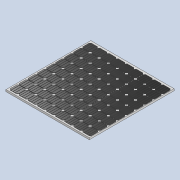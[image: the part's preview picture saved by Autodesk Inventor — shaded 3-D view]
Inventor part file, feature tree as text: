
AUTODESK INVENTOR PART (.ipt)
format: ipt  version: 2021 (Build 250183000, 183)  size: 2,114,048 bytes
history: native  units: in
note: dims shown in document units (in); Inventor stores cm internally (conversion verified against a paired STEP export)
features: extrude x2, plane x2, split x2, sketch x2, direct_edit x1, mirror x1, projected_geometry x1, other x1
ambient origin geometry x8: Origin, YZ Plane, XZ Plane, XY Plane, X Axis, Y Axis, Z Axis, Center Point
bodies: Solid1 (feature_tree)
feature tree (12):
  extrude  "Extrusion1"  Depth=62.5984in
  extrude  "Extrusion2"  Depth=0.0164in
  direct_edit  "Direct Edit1"
  plane  "Work Plane2"
  split  "Split2"
  mirror  "Mirror2"
  plane  "Work Plane3"
  split  "Split3"
  sketch  "Sketch1"  dims[d0=62.5984in d1=41.4567in]
  sketch  "Sketch2"  dims[d2=1.5748in d3=0.0in d5=6.2992in d6=6.2992in d7=0.7874in d8=0.7874in d9=0.7874in d10=0.7874in d11=0.7874in d12=0.7874in d13=0.7874in d14=0.7874in d15=1.1811in d16=0.1969in d17=0.1969in d18=0.1969in d19=2.3622in d21=6.6929in d22=3.5433in d24=6.6929in d27=0.1969in d28=0.0in d29=0.0164in d30=0.3937in d31=0.3937in d33=0.0093in d34=0.0in]
  projected_geometry  "Projected Loop1"
  other  "Scale1"
